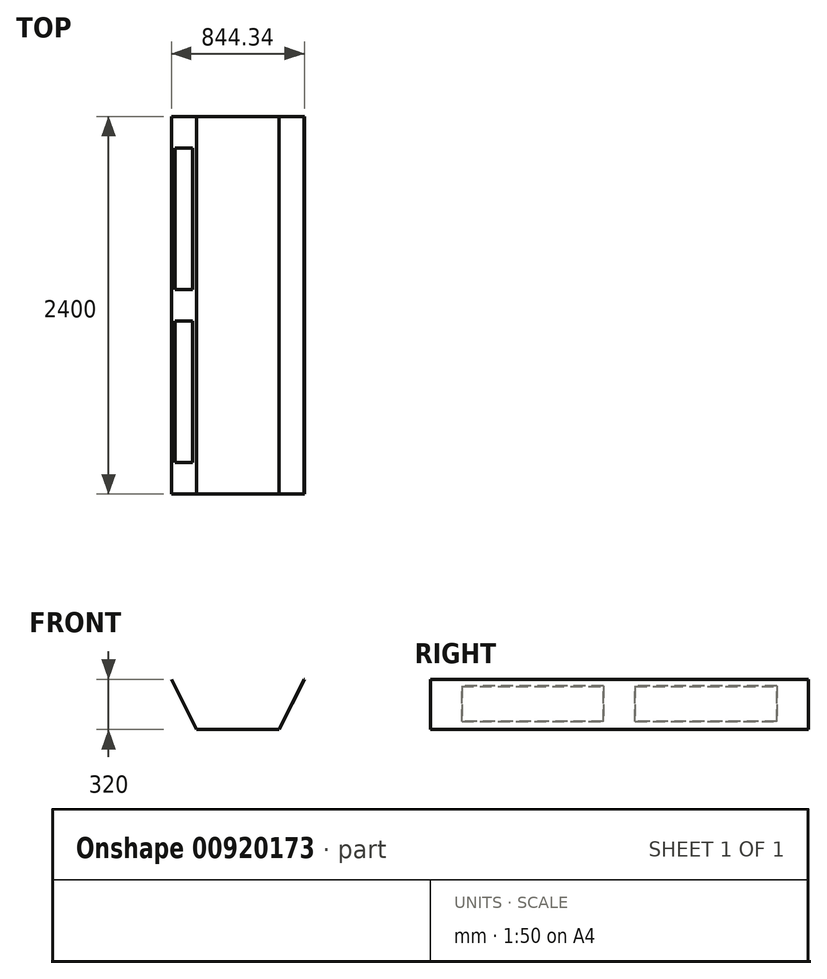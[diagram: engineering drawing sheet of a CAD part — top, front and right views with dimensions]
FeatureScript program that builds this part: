
annotation { "Feature Type Name" : "Feature", "Feature Type Description" : "" }
export const myFeature = defineFeature(function(context is Context, id is Id, definition is map)
    precondition{}
    {
        {
            var Q0;
            Q0=qCreatedBy(makeId("Front.planeOp"),FACE);
            var sketch = newSketch(context, id + "F0", { "sketchPlane" : qUnion([Q0])});
            skLineSegment(sketch, "E0.0", {"start": v(-388.22, 157.92) * mm, "end": v(-239.02, -140.48) * mm});
            skLineSegment(sketch, "E1.0", {"start": v(-221.13, -151.53) * mm, "end": v(276.9, -151.53) * mm});
            skLineSegment(sketch, "E2.0", {"start": v(443.98, 157.92) * mm, "end": v(294.78, -140.48) * mm});
            skLineSegment(sketch, "E3", {"start": v(-388.22, 157.92) * mm, "end": v(-392.7, 166.87) * mm});
            skLineSegment(sketch, "E4", {"start": v(443.98, 157.92) * mm, "end": v(448.45, 166.87) * mm});
            skLineSegment(sketch, "E5", {"start": v(-239.02, -140.48) * mm, "end": v(-233.5, -151.53) * mm});
            skLineSegment(sketch, "E6", {"start": v(-221.13, -151.53) * mm, "end": v(-233.5, -151.53) * mm});
            skLineSegment(sketch, "E7", {"start": v(276.9, -151.53) * mm, "end": v(289.25, -151.53) * mm});
            skLineSegment(sketch, "E8", {"start": v(294.78, -140.48) * mm, "end": v(289.25, -151.53) * mm});
            skLineSegment(sketch, "E9", {"start": v(-392.7, 166.87) * mm, "end": v(-394.3, 166.87) * mm});
            skLineSegment(sketch, "E10", {"start": v(-394.3, 166.87) * mm, "end": v(-234.3, -153.13) * mm});
            skLineSegment(sketch, "E11", {"start": v(448.45, 166.87) * mm, "end": v(450.05, 166.87) * mm});
            skLineSegment(sketch, "E12", {"start": v(450.05, 166.87) * mm, "end": v(290.05, -153.13) * mm});
            skLineSegment(sketch, "E13", {"start": v(290.05, -153.13) * mm, "end": v(-234.3, -153.13) * mm});
            skSolve(sketch);
        }
        {
            var Q0;
            Q0=qSketchRegion(id+"F0",true);
            extrude(context, id + "F1", {"entities" : qUnion([Q0]), "depth" : 2400 * mm, "offsetDistance" : 25 * mm});
        }
        {
            var Q0;
            Q0=makeQuery(id+"F1.opExtrude","SWEPT_FACE",FACE,{"disambiguationData":[OSD([sQuery(id+"F0.wireOp",EDGE,"E10")])]});
            var sketch = newSketch(context, id + "F2", { "sketchPlane" : qUnion([Q0])});
            skLineSegment(sketch, "E14", {"start": v(2200, 275.58) * mm, "end": v(2200, 25.58) * mm});
            skLineSegment(sketch, "E15", {"start": v(2200, 25.58) * mm, "end": v(1300, 25.58) * mm});
            skLineSegment(sketch, "E16", {"start": v(2200, 275.58) * mm, "end": v(1300, 275.58) * mm});
            skLineSegment(sketch, "E17", {"start": v(1300, 275.58) * mm, "end": v(1300, 25.58) * mm});
            skSolve(sketch);
        }
        {
            var Q0;
            Q0=makeQuery(id+"F2.imprint","IMPRINT",FACE,{"disambiguationData":[TD([[makeQuery(id+"F2.imprint","IMPRINT",EDGE,{"derivedFrom":sQuery(id+"F2.wireOp",EDGE,"E14")}),-1.0]])]});
            extrude(context, id + "F3", {"entities" : qUnion([Q0]), "operationType" : NewBodyOperationType.REMOVE, "oppositeDirection" : true, "depth" : 1.6 * mm, "offsetDistance" : 25 * mm});
        }
        {
            var Q0;
            Q0=makeQuery(id+"F1.opExtrude","SWEPT_FACE",FACE,{"disambiguationData":[OSD([sQuery(id+"F0.wireOp",EDGE,"E10")])]});
            var sketch = newSketch(context, id + "F4", { "sketchPlane" : qUnion([Q0])});
            skLineSegment(sketch, "E18", {"start": v(200, 275.58) * mm, "end": v(200, 25.58) * mm});
            skLineSegment(sketch, "E19", {"start": v(200, 25.58) * mm, "end": v(1100, 25.58) * mm});
            skLineSegment(sketch, "E20", {"start": v(1100, 25.58) * mm, "end": v(1100, 275.58) * mm});
            skLineSegment(sketch, "E21", {"start": v(1100, 275.58) * mm, "end": v(200, 275.58) * mm});
            skSolve(sketch);
        }
        {
            var Q0;
            Q0=makeQuery(id+"F4.imprint","IMPRINT",FACE,{"disambiguationData":[TD([[makeQuery(id+"F4.imprint","IMPRINT",EDGE,{"derivedFrom":sQuery(id+"F4.wireOp",EDGE,"E18")}),1.0]])]});
            extrude(context, id + "F5", {"entities" : qUnion([Q0]), "operationType" : NewBodyOperationType.REMOVE, "oppositeDirection" : true, "depth" : 1.6 * mm, "offsetDistance" : 25 * mm});
        }
    });
